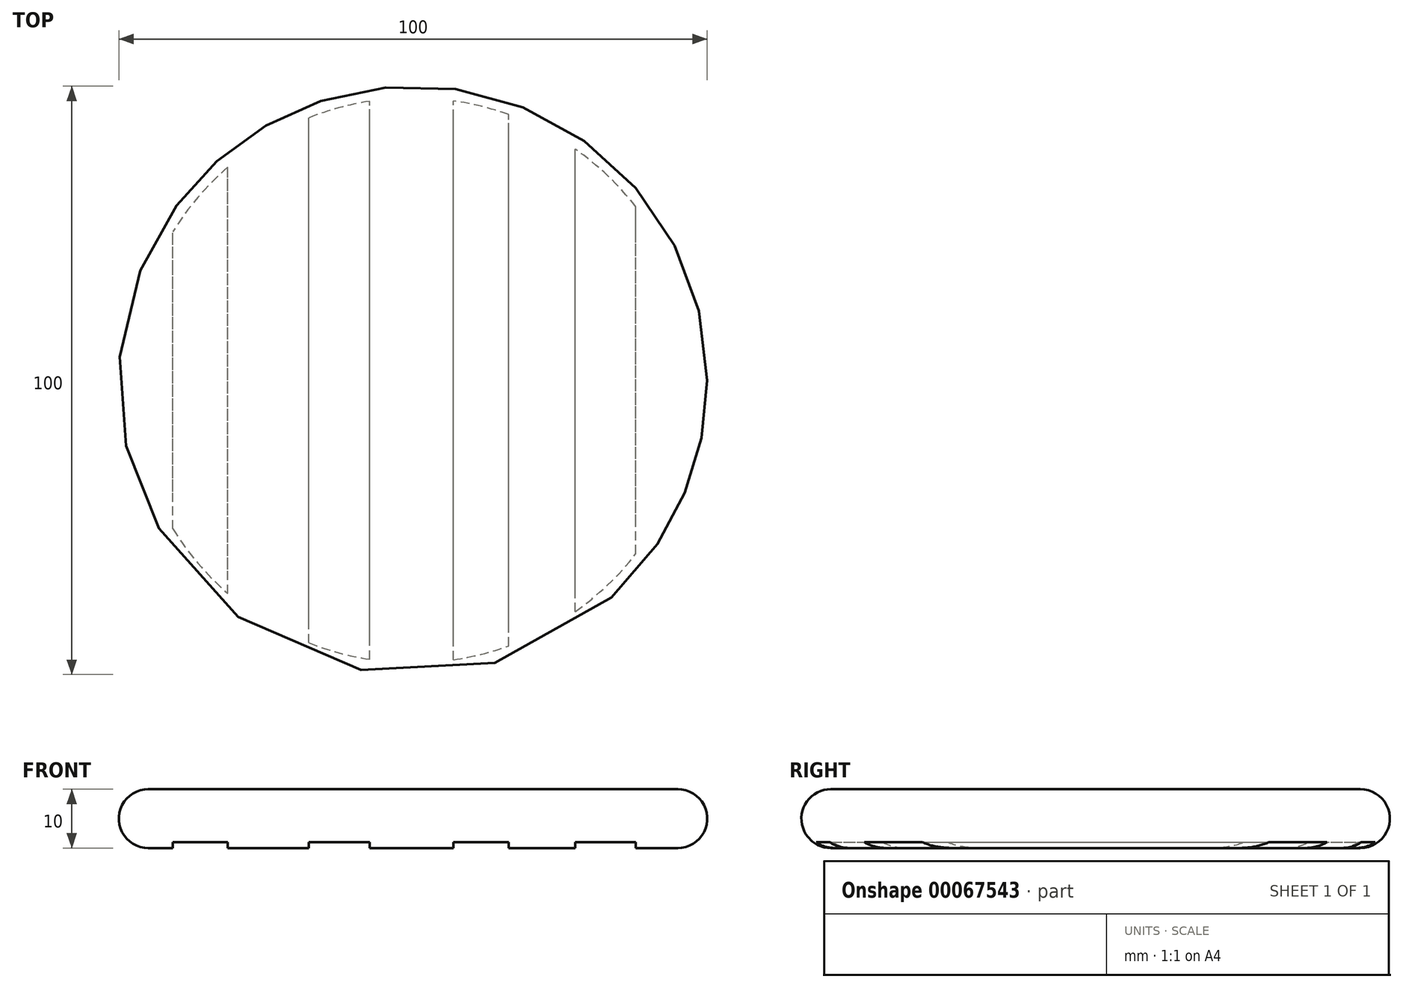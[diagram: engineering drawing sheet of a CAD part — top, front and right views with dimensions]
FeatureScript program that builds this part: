
annotation { "Feature Type Name" : "Feature", "Feature Type Description" : "" }
export const myFeature = defineFeature(function(context is Context, id is Id, definition is map)
    precondition{}
    {
        {
            var Q0;
            Q0=qCreatedBy(makeId("Top.planeOp"),FACE);
            var sketch = newSketch(context, id + "F0", { "sketchPlane" : qUnion([Q0])});
            skPoint(sketch, "E0.rect.middle", {"position": v(0, 0) * mm});
            skPoint(sketch, "E0.rect.top.end.orphan", {"position": v(-17.93, -17.93) * mm});
            skPoint(sketch, "E0.rect.left.end.orphan", {"position": v(17.93, -17.93) * mm});
            skPoint(sketch, "E0.rect.bottom.end.orphan", {"position": v(-17.93, 17.93) * mm});
            skPoint(sketch, "E0.rect.bottom.start.orphan", {"position": v(17.93, 17.93) * mm});
            skCircle(sketch, "E1", {"center": v(0, 0) * mm, "radius": 50 * mm});
            skSolve(sketch);
        }
        {
            var Q0;
            Q0 = qSketchRegion(id + "F0", true);
            extrude(context, id + "F1", {"entities" : qUnion([Q0]), "depth" : 10 * mm});
        }
        {
            var Q0;
            Q0=makeQuery(id+"F1.opExtrude","CAP_FACE",FACE,{"disambiguationData":[OSD([sQuery(id+"F0.wireOp",EDGE,"E1")])],"isStart":true});
            var Q1;
            Q1=makeQuery(id+"F1.opExtrude","CAP_FACE",FACE,{"disambiguationData":[OSD([sQuery(id+"F0.wireOp",EDGE,"E1")])],"isStart":false});
            fillet(context, id + "F2", {"entities" : qUnion([Q0, Q1]), "radius" : 5 * mm, "tangentPropagation" : true, "allowEdgeOverflow" : false});
        }
        {
            var Q0;
            Q0=makeQuery(id+"F1.opExtrude","CAP_FACE",FACE,{"disambiguationData":[OSD([sQuery(id+"F0.wireOp",EDGE,"E1")])],"isStart":true});
            var sketch = newSketch(context, id + "F3", { "sketchPlane" : qUnion([Q0])});
            skLineSegment(sketch, "E2.bottom", {"start": v(-40.82, 56.07) * mm, "end": v(-31.48, 56.07) * mm});
            skLineSegment(sketch, "E2.top", {"start": v(-40.82, -58.53) * mm, "end": v(-31.48, -58.53) * mm});
            skLineSegment(sketch, "E2.left", {"start": v(-40.82, 56.07) * mm, "end": v(-40.82, -58.53) * mm});
            skLineSegment(sketch, "E2.right", {"start": v(-31.48, 56.07) * mm, "end": v(-31.48, -58.53) * mm});
            skLineSegment(sketch, "E3.bottom", {"start": v(-17.7, 56.07) * mm, "end": v(-7.38, 56.07) * mm});
            skLineSegment(sketch, "E3.top", {"start": v(-17.7, -59.51) * mm, "end": v(-7.38, -59.51) * mm});
            skLineSegment(sketch, "E3.left", {"start": v(-17.7, 56.07) * mm, "end": v(-17.7, -59.51) * mm});
            skLineSegment(sketch, "E3.right", {"start": v(-7.38, 56.07) * mm, "end": v(-7.38, -59.51) * mm});
            skLineSegment(sketch, "E4.bottom", {"start": v(6.89, 56.56) * mm, "end": v(16.23, 56.56) * mm});
            skLineSegment(sketch, "E4.top", {"start": v(6.89, -60.99) * mm, "end": v(16.23, -60.99) * mm});
            skLineSegment(sketch, "E4.left", {"start": v(6.89, 56.56) * mm, "end": v(6.89, -60.99) * mm});
            skLineSegment(sketch, "E4.right", {"start": v(16.23, 56.56) * mm, "end": v(16.23, -60.99) * mm});
            skLineSegment(sketch, "E5.bottom", {"start": v(27.54, 55.58) * mm, "end": v(37.87, 55.58) * mm});
            skLineSegment(sketch, "E5.top", {"start": v(27.54, -61.48) * mm, "end": v(37.87, -61.48) * mm});
            skLineSegment(sketch, "E5.left", {"start": v(27.54, 55.58) * mm, "end": v(27.54, -61.48) * mm});
            skLineSegment(sketch, "E5.right", {"start": v(37.87, 55.58) * mm, "end": v(37.87, -61.48) * mm});
            skSolve(sketch);
        }
        {
            var Q0;
            Q0 = qSketchRegion(id + "F3", true);
            extrude(context, id + "F4", {"entities" : qUnion([Q0]), "operationType" : NewBodyOperationType.REMOVE, "oppositeDirection" : true, "depth" : 1 * mm});
        }
    });
